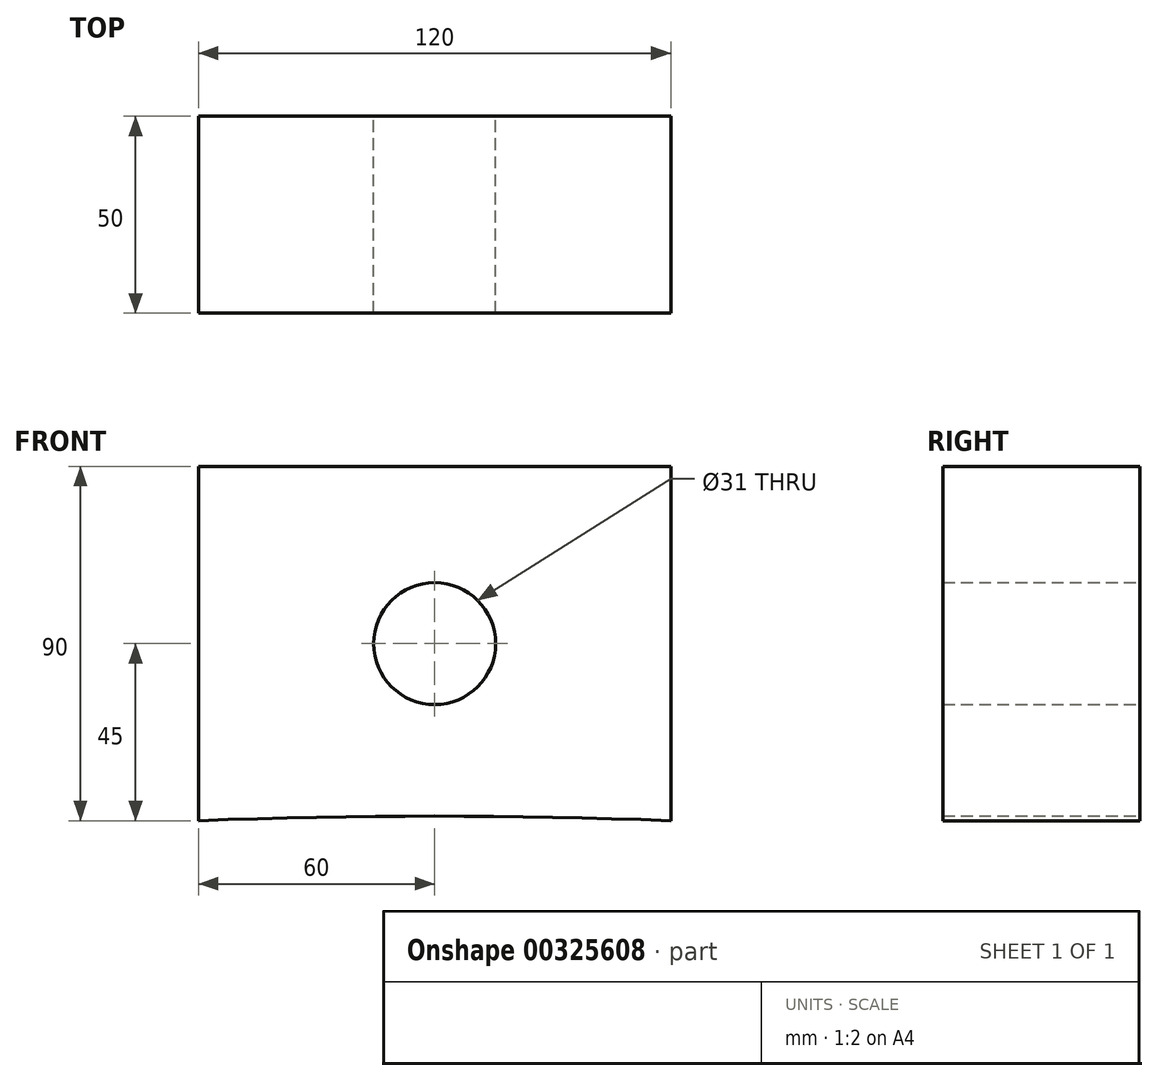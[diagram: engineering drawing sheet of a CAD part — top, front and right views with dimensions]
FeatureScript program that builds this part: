
annotation { "Feature Type Name" : "Feature", "Feature Type Description" : "" }
export const myFeature = defineFeature(function(context is Context, id is Id, definition is map)
    precondition{}
    {
        {
            var Q0;
            Q0=qCreatedBy(makeId("Front.planeOp"),FACE);
            var sketch = newSketch(context, id + "F0", { "sketchPlane" : qUnion([Q0])});
            skLineSegment(sketch, "E0.bottom", {"start": v(-60, 45) * mm, "end": v(60, 45) * mm});
            skLineSegment(sketch, "E0.left", {"start": v(-60, 45) * mm, "end": v(-60, -45) * mm});
            skLineSegment(sketch, "E0.right", {"start": v(60, 45) * mm, "end": v(60, -45) * mm});
            skCircle(sketch, "E1", {"center": v(0, 0) * mm, "radius": 15.5 * mm});
            skPoint(sketch, "E1.centerSnap0", {"position": v(60, 0) * mm});
            skPoint(sketch, "E1.centerSnap1", {"position": v(0, 45) * mm});
            skArc(sketch, "E2", {"start": v(60, -45) * mm, "mid": v(0, -43.83) * mm, "end": v(-60, -45) * mm});
            skPoint(sketch, "E2.third.point", {"position": v(70.8, -3120.2) * mm});
            skSolve(sketch);
        }
        {
            var Q0;
            Q0=makeQuery(id+"F0.imprint","IMPRINT",FACE,{"disambiguationData":[TD([[makeQuery(id+"F0.imprint","IMPRINT",EDGE,{"derivedFrom":sQuery(id+"F0.wireOp",EDGE,"E0.bottom")}),-1.0]])]});
            extrude(context, id + "F1", {"entities" : qUnion([Q0]), "depth" : 50 * mm, "offsetDistance" : 25 * mm});
        }
    });
